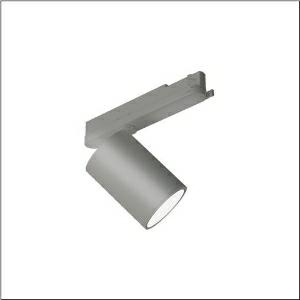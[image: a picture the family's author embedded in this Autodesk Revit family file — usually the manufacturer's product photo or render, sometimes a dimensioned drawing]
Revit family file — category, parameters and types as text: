
# Revit family: spot_31_51sf64mad4b
name_source: partatom
category: Lighting Fixtures
units: mm (PartAtom-declared; Revit-internal decimal feet)

## family parameters
Cut with Voids When Loaded = No
Host = Face
Light Source = No
Part Type = Normal
Room Calculation Point = No
Round Connector Dimension = Use Diameter
Shared = No

## types (1)
- --- (1 x LED, 5250 lm, 41.4 W, 4000K)
    Apparent Load = 41 VA
    CIE Flux Codes = 93 97 100 100 100
    Color Rendering = 90
    Color Temperature = 4000K
    Default Elevation = 1800 mm
    Description = Spot 31, directional spotlight, light control with lens, of PMMA, LED rated luminous flux: 5.040lm, light colour: 940, control gear: ECG Multilumen, with 3-phase adapter, mains connection: 220..240V, AC, 50/60Hz, of aluminium, metallic grey (RAL 9006), length: 213mm, diameter: 90mm, protection rating (complete): IP20, insulation class (complete): insulation class I (protective earthing), certification: CE, impact resistance: IK02, permissible ambient temperature for indoor applications: -20..+40°C, packaging unit: 1 piece
    Height = 175 mm
    Lamp = 1 x LED
    Lamp Light Flux = 5250 lm
    Lamp Power = 41.4 W
    Lamp count = 1
    Length = 90 mm
    Luminous efficacy = 127 lm/W
    Manufacturer = Siteco
    ModVariant = No
    Model = 51SF64MAD4B
    Mounting Place = Ceiling
    Mounting Type = Pendant
    Number of Poles = 1
    OnlyDefault = Yes
    Power Factor = 1
    Product Name = Spot 31
    Product group = directional spotlight
    ProductGroupID = 905
    Protection Class = Protection class I
    Protection Degree = IP 20
    RLX_Detail_Level = 1
    RLX_Emergency_Light_Flux = 0 lm
    RLX_Emergency_Type = 0
    RLX_Emergency_Type_DB = No
    RlxData = <blob elided: 20085 chars, md5=960945bb>
    Socket = socket
    Standby Power = 0 W
    System Light Flux = 5250 lm
    System Power = 41 W
    Type Comments = factory setting: luminous flux: 100 % | (ON | ON | ON | ON) | 1050 mA
    Type Image = l_1273725.jpg
    URL = http://relux.com
    VarID = @adj_167657
    Voltage = 0 V
    Weight = 0.00 kg
    Width = 0 mm  [stored 0 ft]

note: [stored X ft] marks values corroborated as IEEE doubles in the binary element streams (Revit-internal decimal feet)

## geometry (parser evidence)
native form markers: Blend x4, Sweep x9
no freeform markers — native parametric forms only
